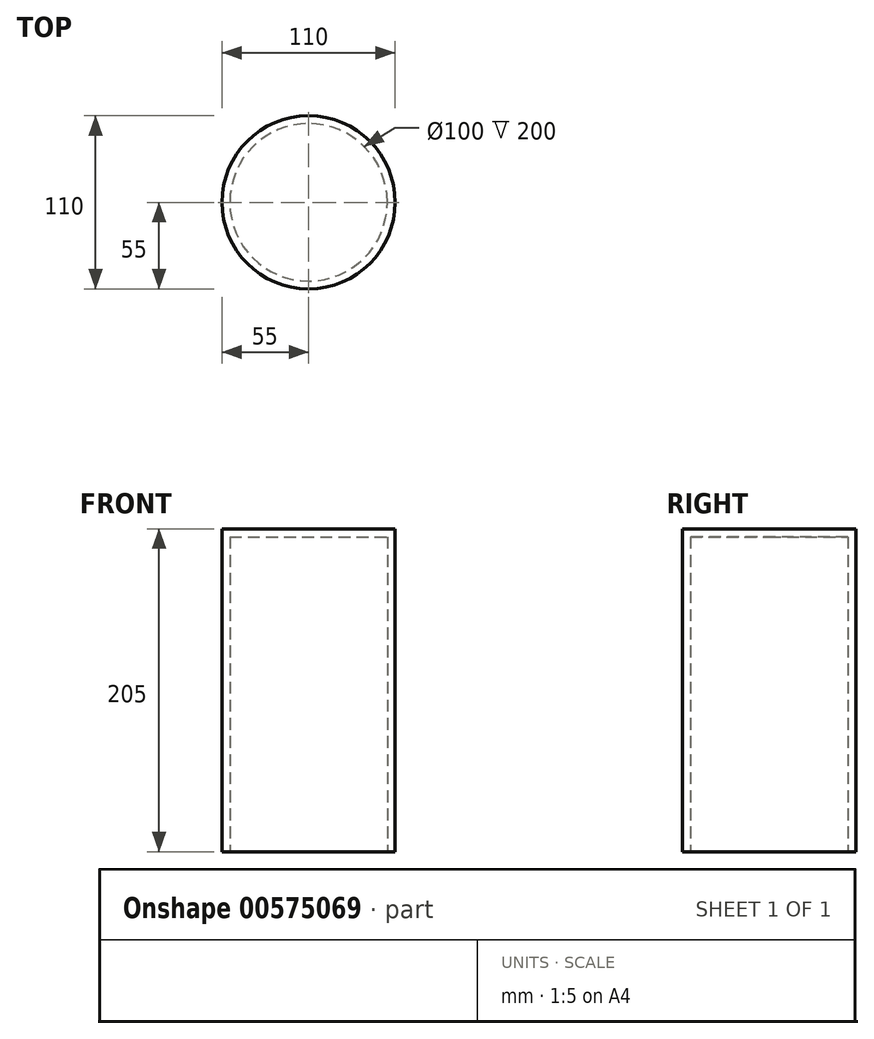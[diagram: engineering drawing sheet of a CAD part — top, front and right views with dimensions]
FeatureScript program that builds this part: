
annotation { "Feature Type Name" : "Feature", "Feature Type Description" : "" }
export const myFeature = defineFeature(function(context is Context, id is Id, definition is map)
    precondition{}
    {
        {
            var Q0;
            Q0=qCreatedBy(makeId("Top.planeOp"),FACE);
            var sketch = newSketch(context, id + "F0", { "sketchPlane" : qUnion([Q0])});
            skCircle(sketch, "E0", {"center": v(0, 0) * mm, "radius": 55 * mm});
            skSolve(sketch);
        }
        {
            var Q0;
            Q0=makeQuery(id+"F0.imprint","IMPRINT",FACE,{"disambiguationData":[TD([[makeQuery(id+"F0.imprint","IMPRINT",EDGE,{"derivedFrom":sQuery(id+"F0.wireOp",EDGE,"E0")}),1.0]])]});
            var Q1;
            Q1=sQuery(id+"F0.wireOp",EDGE,"E0");
            extrude(context, id + "F1", {"entities" : qUnion([Q0]), "surfaceEntities" : qUnion([Q1]), "oppositeDirection" : true, "depth" : 205 * mm, "offsetDistance" : 25 * mm});
        }
        {
            var Q0;
            Q0=makeQuery(id+"F1.opExtrude","CAP_FACE",FACE,{"disambiguationData":[OSD([sQuery(id+"F0.wireOp",EDGE,"E0")])],"isStart":false});
            var sketch = newSketch(context, id + "F2", { "sketchPlane" : qUnion([Q0])});
            skCircle(sketch, "E1", {"center": v(0, 0) * mm, "radius": 50 * mm});
            skSolve(sketch);
        }
        {
            var Q0;
            Q0=makeQuery(id+"F2.imprint","IMPRINT",FACE,{"disambiguationData":[TD([[makeQuery(id+"F2.imprint","IMPRINT",EDGE,{"derivedFrom":sQuery(id+"F2.wireOp",EDGE,"E1")}),1.0]])]});
            var Q1;
            Q1=sQuery(id+"F2.wireOp",EDGE,"E1");
            extrude(context, id + "F3", {"entities" : qUnion([Q0]), "operationType" : NewBodyOperationType.REMOVE, "surfaceEntities" : qUnion([Q1]), "oppositeDirection" : true, "depth" : 200 * mm, "offsetDistance" : 25 * mm});
        }
    });
